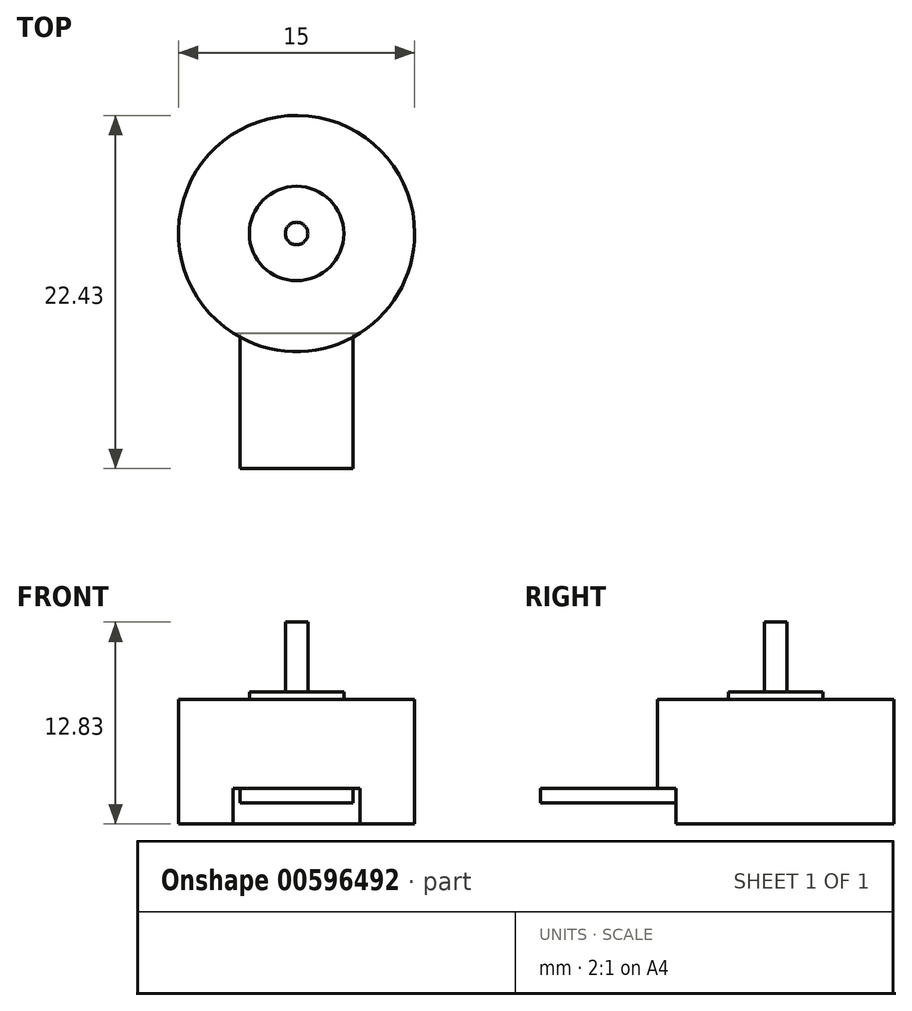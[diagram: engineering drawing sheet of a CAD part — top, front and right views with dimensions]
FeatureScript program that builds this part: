
annotation { "Feature Type Name" : "Feature", "Feature Type Description" : "" }
export const myFeature = defineFeature(function(context is Context, id is Id, definition is map)
    precondition{}
    {
        {
            var Q0;
            Q0=qCreatedBy(makeId("Top.planeOp"),FACE);
            var sketch = newSketch(context, id + "F0", { "sketchPlane" : qUnion([Q0])});
            skCircle(sketch, "E0", {"center": v(0, 0) * mm, "radius": 7.5 * mm});
            skCircle(sketch, "E1", {"center": v(0, 0) * mm, "radius": 3 * mm});
            skCircle(sketch, "E2", {"center": v(0, 0) * mm, "radius": 0.72 * mm});
            skLineSegment(sketch, "E3", {"start": v(-4.04, -6.32) * mm, "end": v(4.04, -6.32) * mm});
            skLineSegment(sketch, "E4", {"start": v(-3.59, -6.32) * mm, "end": v(-3.6, -14.93) * mm});
            skLineSegment(sketch, "E5", {"start": v(-3.6, -14.93) * mm, "end": v(3.6, -14.93) * mm});
            skLineSegment(sketch, "E6", {"start": v(3.6, -14.93) * mm, "end": v(3.59, -6.32) * mm});
            skSolve(sketch);
        }
        {
            var Q0;
            {var subQ0=sQuery(id+"F0.wireOp",EDGE,"E3");var subQ1=sQuery(id+"F0.wireOp",EDGE,"E0");var subQ2=makeQuery(id+"F0.imprint","INTERSECT",VERTEX,{"disambiguationData":[OD(1.0)],"derivedFrom":[subQ1,subQ0]});Q0=makeQuery(id+"F0.imprint","IMPRINT",FACE,{"disambiguationData":[TD([[makeQuery(id+"F0.imprint","IMPRINT",EDGE,{"disambiguationData":[TD([[subQ2,1.0]])],"derivedFrom":subQ1}),1.0]])]});}
            var Q1;
            {var subQ0=sQuery(id+"F0.wireOp",EDGE,"E4");var subQ1=sQuery(id+"F0.wireOp",EDGE,"E0");var subQ2=makeQuery(id+"F0.imprint","INTERSECT",VERTEX,{"derivedFrom":[subQ1,subQ0]});Q1=makeQuery(id+"F0.imprint","IMPRINT",FACE,{"disambiguationData":[TD([[makeQuery(id+"F0.imprint","IMPRINT",EDGE,{"disambiguationData":[TD([[subQ2,-1.0]])],"derivedFrom":subQ1}),1.0]])]});}
            var Q2;
            {var subQ0=sQuery(id+"F0.wireOp",EDGE,"E3");var subQ1=sQuery(id+"F0.wireOp",EDGE,"E0");var subQ2=makeQuery(id+"F0.imprint","INTERSECT",VERTEX,{"disambiguationData":[OD(0.0)],"derivedFrom":[subQ1,subQ0]});Q2=makeQuery(id+"F0.imprint","IMPRINT",FACE,{"disambiguationData":[TD([[makeQuery(id+"F0.imprint","IMPRINT",EDGE,{"disambiguationData":[TD([[subQ2,-1.0]])],"derivedFrom":subQ1}),1.0]])]});}
            var Q3;
            Q3=makeQuery(id+"F0.imprint","IMPRINT",FACE,{"disambiguationData":[TD([[makeQuery(id+"F0.imprint","IMPRINT",EDGE,{"derivedFrom":sQuery(id+"F0.wireOp",EDGE,"E1")}),-1.0]])]});
            var Q4;
            Q4=makeQuery(id+"F0.imprint","IMPRINT",FACE,{"disambiguationData":[TD([[makeQuery(id+"F0.imprint","IMPRINT",EDGE,{"derivedFrom":sQuery(id+"F0.wireOp",EDGE,"E2")}),1.0]])]});
            var Q5;
            Q5=makeQuery(id+"F0.imprint","IMPRINT",FACE,{"disambiguationData":[TD([[makeQuery(id+"F0.imprint","IMPRINT",EDGE,{"derivedFrom":sQuery(id+"F0.wireOp",EDGE,"E1")}),1.0]])]});
            extrude(context, id + "F1", {"entities" : qUnion([Q0, Q1, Q2, Q3, Q4, Q5]), "depth" : 5.67 * mm, "offsetDistance" : 25 * mm});
        }
        {
            var Q0;
            Q0=makeQuery(id+"F0.imprint","IMPRINT",FACE,{"disambiguationData":[TD([[makeQuery(id+"F0.imprint","IMPRINT",EDGE,{"derivedFrom":sQuery(id+"F0.wireOp",EDGE,"E1")}),1.0]])]});
            var Q1;
            Q1=makeQuery(id+"F0.imprint","IMPRINT",FACE,{"disambiguationData":[TD([[makeQuery(id+"F0.imprint","IMPRINT",EDGE,{"derivedFrom":sQuery(id+"F0.wireOp",EDGE,"E2")}),1.0]])]});
            extrude(context, id + "F2", {"entities" : qUnion([Q0, Q1]), "operationType" : NewBodyOperationType.ADD, "depth" : 6.15 * mm, "offsetDistance" : 25 * mm});
        }
        {
            var Q0;
            Q0=makeQuery(id+"F0.imprint","IMPRINT",FACE,{"disambiguationData":[TD([[makeQuery(id+"F0.imprint","IMPRINT",EDGE,{"derivedFrom":sQuery(id+"F0.wireOp",EDGE,"E2")}),1.0]])]});
            extrude(context, id + "F3", {"entities" : qUnion([Q0]), "operationType" : NewBodyOperationType.ADD, "depth" : 10.58 * mm, "offsetDistance" : 25 * mm});
        }
        {
            var Q0;
            Q0=makeQuery(id+"F0.imprint","IMPRINT",FACE,{"disambiguationData":[TD([[makeQuery(id+"F0.imprint","IMPRINT",EDGE,{"derivedFrom":sQuery(id+"F0.wireOp",EDGE,"E2")}),1.0]])]});
            var Q1;
            Q1=makeQuery(id+"F0.imprint","IMPRINT",FACE,{"disambiguationData":[TD([[makeQuery(id+"F0.imprint","IMPRINT",EDGE,{"derivedFrom":sQuery(id+"F0.wireOp",EDGE,"E1")}),1.0]])]});
            var Q2;
            Q2=makeQuery(id+"F0.imprint","IMPRINT",FACE,{"disambiguationData":[TD([[makeQuery(id+"F0.imprint","IMPRINT",EDGE,{"derivedFrom":sQuery(id+"F0.wireOp",EDGE,"E1")}),-1.0]])]});
            extrude(context, id + "F4", {"entities" : qUnion([Q0, Q1, Q2]), "operationType" : NewBodyOperationType.ADD, "oppositeDirection" : true, "depth" : 2.25 * mm, "offsetDistance" : 25 * mm});
        }
        {
            var Q0;
            {var subQ0=sQuery(id+"F0.wireOp",EDGE,"E4");var subQ1=sQuery(id+"F0.wireOp",EDGE,"E0");var subQ2=makeQuery(id+"F0.imprint","INTERSECT",VERTEX,{"derivedFrom":[subQ1,subQ0]});Q0=makeQuery(id+"F0.imprint","IMPRINT",FACE,{"disambiguationData":[TD([[makeQuery(id+"F0.imprint","IMPRINT",EDGE,{"disambiguationData":[TD([[subQ2,-1.0]])],"derivedFrom":subQ1}),1.0]])]});}
            var Q1;
            {var subQ5=sQuery(id+"F0.wireOp",EDGE,"E5");Q1=makeQuery(id+"F0.imprint","IMPRINT",FACE,{"disambiguationData":[TD([[makeQuery(id+"F0.imprint","IMPRINT",EDGE,{"derivedFrom":subQ5}),1.0]])]});}
            extrude(context, id + "F5", {"entities" : qUnion([Q0, Q1]), "operationType" : NewBodyOperationType.ADD, "oppositeDirection" : true, "depth" : 0.91 * mm, "offsetDistance" : 25 * mm});
        }
    });
